# Revit family: Taza_Erie
name_source: partatom
category: Aparatos sanitarios
revit_build: Autodesk Revit 2016 (Build: 20151007_0715(x64)
units: mm (PartAtom-declared; Revit-internal decimal feet)

## family parameters
Anfitrión = Muro
Compartido = No
Corte con vacíos al cargar = No
Cota de conector redondo = Diámetro de uso
Número OmniClass = 23.45.05.21.11.11
Punto de cálculo de habitación = No
Siempre vertical = Sí
Tipo de pieza = Normal
Título OmniClass = Water Operated Water Closets

## types (1)
- Tipo 1
    Acabado = Porcelana Brillante
    Alto Nominal = 430 mm
    Altura de Conexión de entrada ADA = 47,82 cm
    Altura de conexión de entrada STD = 42,74 cm
    Altura de conexión sanitaria ADA = 18,2 cm
    Altura de conexión sanitaria STD = 13 cm
    Ancho Nominal = 400 mm  [stored 1.31234 ft]
    Característica = Taza colgada al muro con entrada posterior, con sifón oculto, que genera mayor anti vandalismo, reduce el área de acumulación de mugre .
    Color = Blanco
    Conusmo de agua = 4,85 Lpf / 1,28 GPf
    Cumplimiento de Norma = NTC 920.1 Aparatos sanitarios de porcelana vitrificada / ASME A 112.19.2 / CSA B 45.5 / NOM 009 - 10 / ADA / EPA
    Código de montaje = D2010100
    Descripción de la garantía = Garantía Corona Limitada de por vida para porcelana, Garanía grifería limitada de acuerdo a tipología de grifería y fabricante
    Diámetro de conexión de entrada = 1 1/2"
    Diámetro de conexión sanitaria = 2"
    Duración Garantía Partes = De por vida porcelana, limitada Grifería
    Duración Garantía Unidad = Años
    Fabricante = Corona
    Forma = Ovalada, Alongada
    Imagen de tipo = <Ninguno>
    Longitud Nominal = 660 mm
    Material = Ceramica_Corona_Blanco
    Material Secundario = Plastico_Corona_Blanco
    Modelo = Taza Erie EP Antibacterial para fluxómetro grifería
    Nombre = Taza Erie EP
    Numero de Modelo = 03111A001
    Responsable Garantia Partes = www.corona.com.co
    Tamaño = 66 x 40 x 38 cm Estadanr / 66 x 40 x 43,2 cm ADA
    Tipo de Activo = Fijo
    URL = https://s3.amazonaws.com

note: [stored X ft] marks values corroborated as IEEE doubles in the binary element streams (Revit-internal decimal feet)
